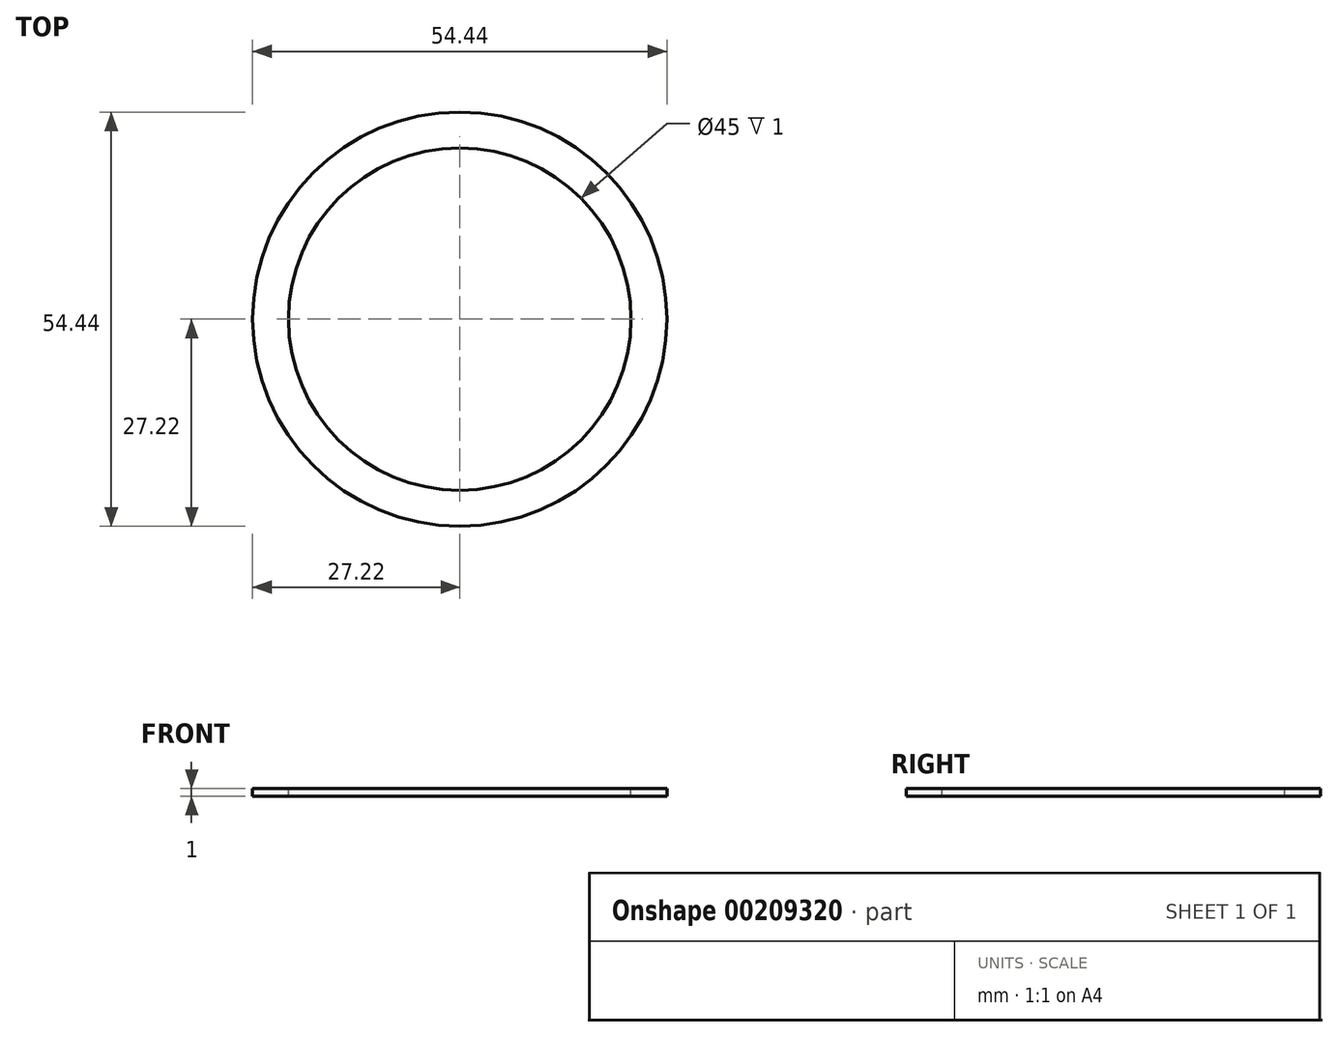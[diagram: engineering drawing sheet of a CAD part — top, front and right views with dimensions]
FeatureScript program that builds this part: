
annotation { "Feature Type Name" : "Feature", "Feature Type Description" : "" }
export const myFeature = defineFeature(function(context is Context, id is Id, definition is map)
    precondition{}
    {
        {
            var Q0;
            Q0=qCreatedBy(makeId("Front.planeOp"),FACE);
            var sketch = newSketch(context, id + "F0", { "sketchPlane" : qUnion([Q0])});
            skPoint(sketch, "E0", {"position": v(0, 0) * mm});
            skPoint(sketch, "E1", {"position": v(0, -22) * mm});
            skPoint(sketch, "E2", {"position": v(27.22, -22) * mm});
            skArc(sketch, "E3", {"start": v(27.22, -22) * mm, "mid": v(33, -11.67) * mm, "end": v(35, 0) * mm});
            skLineSegment(sketch, "E4", {"start": v(0, 0) * mm, "end": v(0, -22) * mm, "construction": true});
            skArc(sketch, "E5", {"start": v(36, 0) * mm, "mid": v(34.07, -11.62) * mm, "end": v(28.5, -22) * mm});
            skLineSegment(sketch, "E6", {"start": v(36, 0) * mm, "end": v(35, 0) * mm});
            skLineSegment(sketch, "E7", {"start": v(28.5, -22) * mm, "end": v(27.22, -22) * mm});
            skSolve(sketch);
        }
        {
            var Q0;
            Q0=qCreatedBy(makeId("Top.planeOp"),FACE);
            var sketch = newSketch(context, id + "F1", { "sketchPlane" : qUnion([Q0])});
            skCircle(sketch, "E8", {"center": v(0, 0) * mm, "radius": 27.22 * mm});
            skCircle(sketch, "E9", {"center": v(0, 0) * mm, "radius": 22.5 * mm});
            skSolve(sketch);
        }
        {
            var Q0;
            Q0=makeQuery(id+"F1.imprint","IMPRINT",FACE,{"disambiguationData":[TD([[makeQuery(id+"F1.imprint","IMPRINT",EDGE,{"derivedFrom":sQuery(id+"F1.wireOp",EDGE,"E8")}),1.0]])]});
            extrude(context, id + "F2", {"entities" : qUnion([Q0]), "oppositeDirection" : true, "depth" : 22 * mm});
        }
        {
            var Q0;
            Q0=makeQuery(id+"F2.opExtrude","CAP_FACE",FACE,{"disambiguationData":[OSD([sQuery(id+"F1.wireOp",EDGE,"E8"),sQuery(id+"F1.wireOp",EDGE,"E9")])],"isStart":true});
            extrude(context, id + "F3", {"entities" : qUnion([Q0]), "operationType" : NewBodyOperationType.REMOVE, "oppositeDirection" : true, "depth" : 21 * mm});
        }
        {
            var Q0;
            Q0=sQuery(id+"F0.wireOp",EDGE,"E3");
            var Q1;
            Q1=sQuery(id+"F0.wireOp",EDGE,"E5");
            var Q2;
            Q2=sQuery(id+"F0.wireOp",EDGE,"E4");
            revolve(context, id + "F4", {"bodyType" : ToolBodyType.SURFACE, "surfaceEntities" : qUnion([Q0, Q1]), "axis" : qUnion([Q2]), "revolveType" : RevolveType.FULL});
        }
    });
